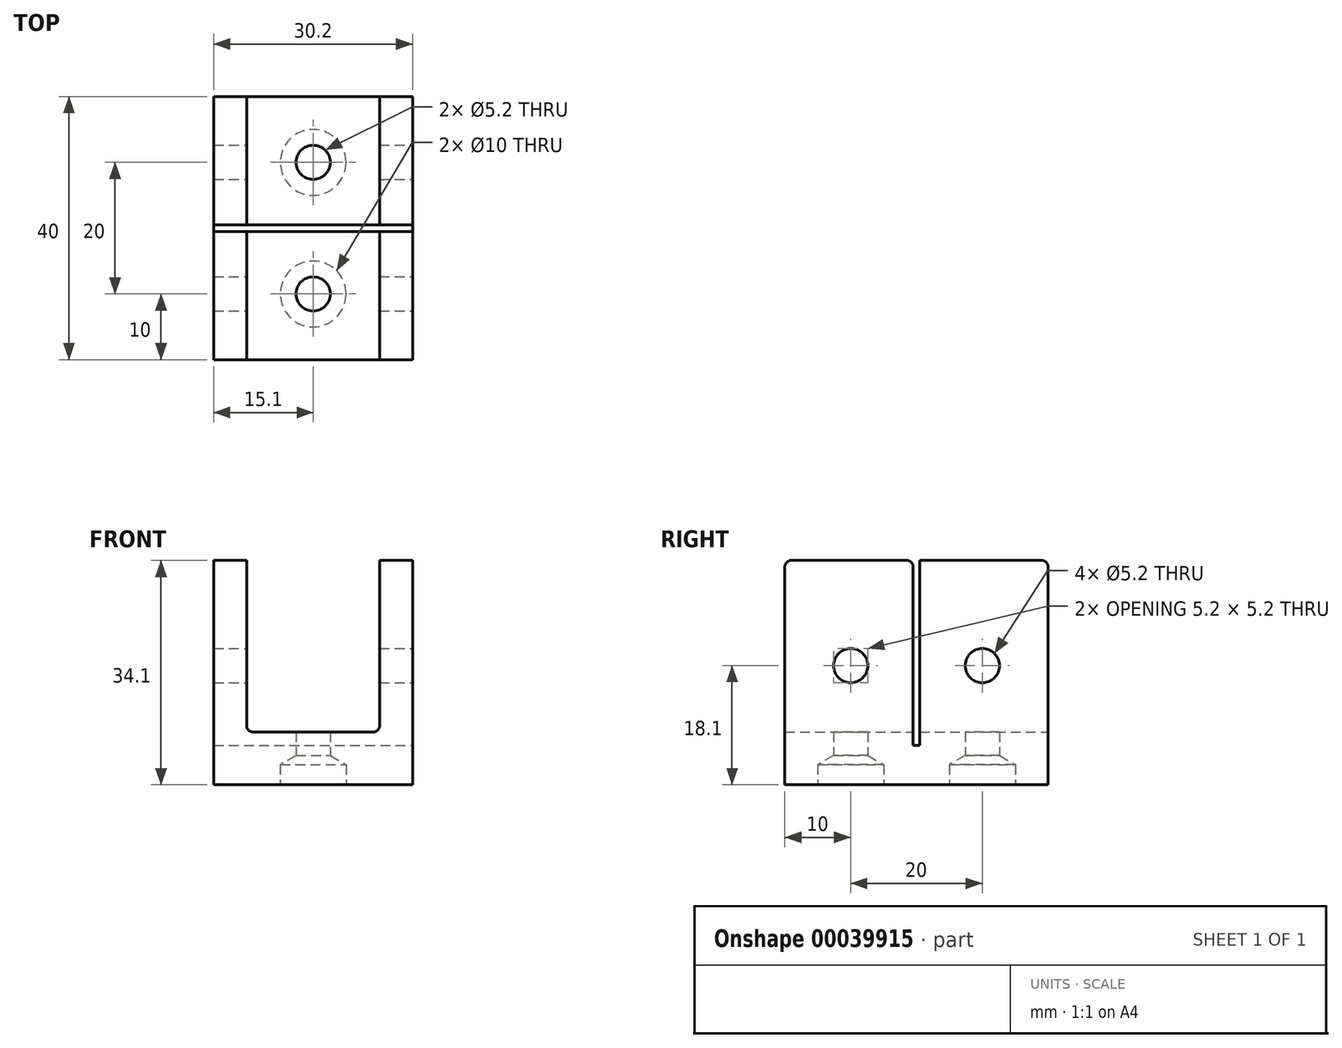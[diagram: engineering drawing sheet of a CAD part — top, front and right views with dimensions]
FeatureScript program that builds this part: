
annotation { "Feature Type Name" : "Feature", "Feature Type Description" : "" }
export const myFeature = defineFeature(function(context is Context, id is Id, definition is map)
    precondition{}
    {
        {
            var Q0;
            Q0=qCreatedBy(makeId("Front.planeOp"),FACE);
            var sketch = newSketch(context, id + "F0", { "sketchPlane" : qUnion([Q0])});
            skLineSegment(sketch, "E0.rect.bottom", {"start": v(10, 10) * mm, "end": v(-10, 10) * mm});
            skLineSegment(sketch, "E0.rect.top", {"start": v(10, -10) * mm, "end": v(-10, -10) * mm});
            skLineSegment(sketch, "E0.rect.left", {"start": v(10, 10) * mm, "end": v(10, -10) * mm});
            skLineSegment(sketch, "E0.rect.right", {"start": v(-10, 10) * mm, "end": v(-10, -10) * mm});
            skPoint(sketch, "E0.rect.middle", {"position": v(0, 0) * mm});
            skSolve(sketch);
        }
        {
            var Q0;
            Q0=qCreatedBy(makeId("Front.planeOp"),FACE);
            var sketch = newSketch(context, id + "F1", { "sketchPlane" : qUnion([Q0])});
            skLineSegment(sketch, "E1", {"start": v(10.1, 16) * mm, "end": v(10.1, -10.1) * mm});
            skLineSegment(sketch, "E2", {"start": v(10.1, -10.1) * mm, "end": v(-10.1, -10.1) * mm});
            skLineSegment(sketch, "E3", {"start": v(-10.1, -10.1) * mm, "end": v(-10.1, 16) * mm});
            skLineSegment(sketch, "E4", {"start": v(-10.1, 16) * mm, "end": v(-15.1, 16) * mm});
            skLineSegment(sketch, "E5", {"start": v(-15.1, 16) * mm, "end": v(-15.1, -18.1) * mm});
            skLineSegment(sketch, "E6", {"start": v(-15.1, -18.1) * mm, "end": v(15.1, -18.1) * mm});
            skLineSegment(sketch, "E7", {"start": v(15.1, -18.1) * mm, "end": v(15.1, 16) * mm});
            skLineSegment(sketch, "E8", {"start": v(15.1, 16) * mm, "end": v(10.1, 16) * mm});
            skLineSegment(sketch, "E9", {"start": v(-10, 0) * mm, "end": v(-10.1, 0) * mm, "construction": true});
            skLineSegment(sketch, "E10", {"start": v(0, -10) * mm, "end": v(0, -10.1) * mm, "construction": true});
            skSolve(sketch);
        }
        {
            var Q0;
            Q0=makeQuery(id+"F1.imprint","IMPRINT",FACE,{"disambiguationData":[TD([[makeQuery(id+"F1.imprint","IMPRINT",EDGE,{"derivedFrom":sQuery(id+"F1.wireOp",EDGE,"E1")}),1.0]])]});
            extrude(context, id + "F2", {"entities" : qUnion([Q0]), "endBound" : BoundingType.SYMMETRIC, "depth" : 40 * mm});
        }
        {
            var Q0;
            Q0=qCreatedBy(makeId("Right.planeOp"),FACE);
            var sketch = newSketch(context, id + "F3", { "sketchPlane" : qUnion([Q0])});
            skLineSegment(sketch, "E11.bottom", {"start": v(0.5, 16) * mm, "end": v(-0.5, 16) * mm});
            skLineSegment(sketch, "E11.top", {"start": v(0.5, -12.1) * mm, "end": v(-0.5, -12.1) * mm});
            skLineSegment(sketch, "E11.left", {"start": v(0.5, 16) * mm, "end": v(0.5, -12.1) * mm});
            skLineSegment(sketch, "E11.right", {"start": v(-0.5, 16) * mm, "end": v(-0.5, -12.1) * mm});
            skLineSegment(sketch, "E12", {"start": v(0.5, 0) * mm, "end": v(-0.5, 0) * mm, "construction": true});
            skSolve(sketch);
        }
        {
            var Q0;
            Q0 = qSketchRegion(id + "F3", true);
            extrude(context, id + "F4", {"entities" : qUnion([Q0]), "operationType" : NewBodyOperationType.REMOVE, "endBound" : BoundingType.THROUGH_ALL, "oppositeDirection" : true, "depth" : 25 * mm, "hasSecondDirection" : true, "secondDirectionBound" : SecondDirectionBoundingType.THROUGH_ALL, "secondDirectionOppositeDirection" : false, "secondDirectionDepth" : 25 * mm});
        }
        {
            var Q0;
            Q0=qCreatedBy(makeId("Right.planeOp"),FACE);
            var sketch = newSketch(context, id + "F5", { "sketchPlane" : qUnion([Q0])});
            skCircle(sketch, "E13", {"center": v(10, 0) * mm, "radius": 2.6 * mm});
            skCircle(sketch, "E14", {"center": v(-10, 0) * mm, "radius": 2.6 * mm});
            skLineSegment(sketch, "E15", {"start": v(10, 0) * mm, "end": v(-10, 0) * mm, "construction": true});
            skSolve(sketch);
        }
        {
            var Q0;
            Q0 = qSketchRegion(id + "F5", true);
            extrude(context, id + "F6", {"entities" : qUnion([Q0]), "operationType" : NewBodyOperationType.REMOVE, "endBound" : BoundingType.THROUGH_ALL, "oppositeDirection" : true, "depth" : 25 * mm, "hasSecondDirection" : true, "secondDirectionBound" : SecondDirectionBoundingType.THROUGH_ALL, "secondDirectionOppositeDirection" : false, "secondDirectionDepth" : 25 * mm});
        }
        {
            var Q0;
            Q0=makeQuery(id+"F2.opExtrude","SWEPT_FACE",FACE,{"disambiguationData":[OSD([sQuery(id+"F1.wireOp",EDGE,"E6")])]});
            var sketch = newSketch(context, id + "F7", { "sketchPlane" : qUnion([Q0])});
            skCircle(sketch, "E16", {"center": v(0, 10) * mm, "radius": 2.6 * mm});
            skCircle(sketch, "E17", {"center": v(0, -10) * mm, "radius": 2.6 * mm});
            skLineSegment(sketch, "E18", {"start": v(0, 10) * mm, "end": v(0, -10) * mm, "construction": true});
            skSolve(sketch);
        }
        {
            var Q0;
            Q0 = qSketchRegion(id + "F7", true);
            extrude(context, id + "F8", {"entities" : qUnion([Q0]), "operationType" : NewBodyOperationType.REMOVE, "endBound" : BoundingType.UP_TO_NEXT, "oppositeDirection" : true, "depth" : 25 * mm});
        }
        {
            var Q0;
            Q0=makeQuery(id+"F2.opExtrude","SWEPT_FACE",FACE,{"disambiguationData":[OSD([sQuery(id+"F1.wireOp",EDGE,"E6")])]});
            var sketch = newSketch(context, id + "F9", { "sketchPlane" : qUnion([Q0])});
            skCircle(sketch, "E19", {"center": v(0, 10) * mm, "radius": 5 * mm});
            skCircle(sketch, "E20", {"center": v(0, -10) * mm, "radius": 5 * mm});
            skSolve(sketch);
        }
        {
            var Q0;
            Q0 = qSketchRegion(id + "F9", true);
            extrude(context, id + "F10", {"entities" : qUnion([Q0]), "operationType" : NewBodyOperationType.REMOVE, "oppositeDirection" : true, "depth" : 3 * mm});
        }
        {
            var Q0;
            Q0=makeQuery(id+"F10.boolean.opBoolean","INTERSECT",EDGE,{"derivedFrom":[makeQuery(id+"F8.boolean.opBoolean","COPY",FACE,{"derivedFrom":makeQuery(id+"F8.opExtrude","SWEPT_FACE",FACE,{"disambiguationData":[OSD([sQuery(id+"F7.wireOp",EDGE,"E16")])]})}),makeQuery(id+"F10.opExtrude","CAP_FACE",FACE,{"disambiguationData":[OSD([sQuery(id+"F9.wireOp",EDGE,"E19")])],"isStart":false})]});
            var Q1;
            Q1=makeQuery(id+"F10.boolean.opBoolean","INTERSECT",EDGE,{"derivedFrom":[makeQuery(id+"F8.boolean.opBoolean","COPY",FACE,{"derivedFrom":makeQuery(id+"F8.opExtrude","SWEPT_FACE",FACE,{"disambiguationData":[OSD([sQuery(id+"F7.wireOp",EDGE,"E17")])]})}),makeQuery(id+"F10.opExtrude","CAP_FACE",FACE,{"disambiguationData":[OSD([sQuery(id+"F9.wireOp",EDGE,"E20")])],"isStart":false})]});
            chamfer(context, id + "F11", {"entities" : qUnion([Q0, Q1]), "chamferType" : ChamferType.OFFSET_ANGLE, "width" : 2.5 * mm, "oppositeDirection" : false, "angle" : 30 * degree, "tangentPropagation" : true});
        }
        {
            var Q0;
            {var subQ0=sQuery(id+"F1.wireOp",EDGE,"E2");var subQ1=sQuery(id+"F1.wireOp",EDGE,"E3");Q0=makeQuery(id+"F4.boolean.opBoolean","SPLIT",EDGE,{"disambiguationData":[TD([makeQuery(id+"F4.opExtrude","SWEPT_FACE",FACE,{"disambiguationData":[OSD([sQuery(id+"F3.wireOp",EDGE,"E11.right")])]})])],"derivedFrom":makeQuery(id+"F2.opExtrude","SWEPT_EDGE",EDGE,{"disambiguationData":[OSD([subQ0,subQ1])]})});}
            var Q1;
            {var subQ0=sQuery(id+"F1.wireOp",EDGE,"E2");var subQ1=sQuery(id+"F1.wireOp",EDGE,"E3");Q1=makeQuery(id+"F4.boolean.opBoolean","SPLIT",EDGE,{"disambiguationData":[TD([makeQuery(id+"F4.opExtrude","SWEPT_FACE",FACE,{"disambiguationData":[OSD([sQuery(id+"F3.wireOp",EDGE,"E11.left")])]})])],"derivedFrom":makeQuery(id+"F2.opExtrude","SWEPT_EDGE",EDGE,{"disambiguationData":[OSD([subQ0,subQ1])]})});}
            var Q2;
            {var subQ0=sQuery(id+"F1.wireOp",EDGE,"E1");var subQ1=sQuery(id+"F1.wireOp",EDGE,"E2");Q2=makeQuery(id+"F4.boolean.opBoolean","SPLIT",EDGE,{"disambiguationData":[TD([makeQuery(id+"F4.opExtrude","SWEPT_FACE",FACE,{"disambiguationData":[OSD([sQuery(id+"F3.wireOp",EDGE,"E11.right")])]})])],"derivedFrom":makeQuery(id+"F2.opExtrude","SWEPT_EDGE",EDGE,{"disambiguationData":[OSD([subQ0,subQ1])]})});}
            var Q3;
            {var subQ0=sQuery(id+"F1.wireOp",EDGE,"E1");var subQ1=sQuery(id+"F1.wireOp",EDGE,"E2");Q3=makeQuery(id+"F4.boolean.opBoolean","SPLIT",EDGE,{"disambiguationData":[TD([makeQuery(id+"F4.opExtrude","SWEPT_FACE",FACE,{"disambiguationData":[OSD([sQuery(id+"F3.wireOp",EDGE,"E11.left")])]})])],"derivedFrom":makeQuery(id+"F2.opExtrude","SWEPT_EDGE",EDGE,{"disambiguationData":[OSD([subQ0,subQ1])]})});}
            var Q4;
            Q4=makeQuery(id+"F2.opExtrude","CAP_EDGE",EDGE,{"disambiguationData":[OSD([sQuery(id+"F1.wireOp",EDGE,"E4")])],"isStart":true});
            var Q5;
            Q5=makeQuery(id+"F4.boolean.opBoolean","COPY",EDGE,{"disambiguationData":[OD(0.0)],"derivedFrom":makeQuery(id+"F4.opExtrude","SWEPT_EDGE",EDGE,{"disambiguationData":[OSD([sQuery(id+"F3.wireOp",EDGE,"E11.bottom"),sQuery(id+"F3.wireOp",EDGE,"E11.left")])]})});
            var Q6;
            Q6=makeQuery(id+"F4.boolean.opBoolean","COPY",EDGE,{"disambiguationData":[OD(0.0)],"derivedFrom":makeQuery(id+"F4.opExtrude","SWEPT_EDGE",EDGE,{"disambiguationData":[OSD([sQuery(id+"F3.wireOp",EDGE,"E11.bottom"),sQuery(id+"F3.wireOp",EDGE,"E11.right")])]})});
            var Q7;
            Q7=makeQuery(id+"F2.opExtrude","CAP_EDGE",EDGE,{"disambiguationData":[OSD([sQuery(id+"F1.wireOp",EDGE,"E4")])],"isStart":false});
            var Q8;
            Q8=makeQuery(id+"F2.opExtrude","CAP_EDGE",EDGE,{"disambiguationData":[OSD([sQuery(id+"F1.wireOp",EDGE,"E8")])],"isStart":true});
            var Q9;
            Q9=makeQuery(id+"F4.boolean.opBoolean","COPY",EDGE,{"disambiguationData":[OD(1.0)],"derivedFrom":makeQuery(id+"F4.opExtrude","SWEPT_EDGE",EDGE,{"disambiguationData":[OSD([sQuery(id+"F3.wireOp",EDGE,"E11.bottom"),sQuery(id+"F3.wireOp",EDGE,"E11.left")])]})});
            var Q10;
            Q10=makeQuery(id+"F4.boolean.opBoolean","COPY",EDGE,{"disambiguationData":[OD(1.0)],"derivedFrom":makeQuery(id+"F4.opExtrude","SWEPT_EDGE",EDGE,{"disambiguationData":[OSD([sQuery(id+"F3.wireOp",EDGE,"E11.bottom"),sQuery(id+"F3.wireOp",EDGE,"E11.right")])]})});
            var Q11;
            Q11=makeQuery(id+"F2.opExtrude","CAP_EDGE",EDGE,{"disambiguationData":[OSD([sQuery(id+"F1.wireOp",EDGE,"E8")])],"isStart":false});
            fillet(context, id + "F12", {"entities" : qUnion([Q0, Q1, Q2, Q3, Q4, Q5, Q6, Q7, Q8, Q9, Q10, Q11]), "radius" : 1 * mm, "tangentPropagation" : true, "allowEdgeOverflow" : false});
        }
    });
